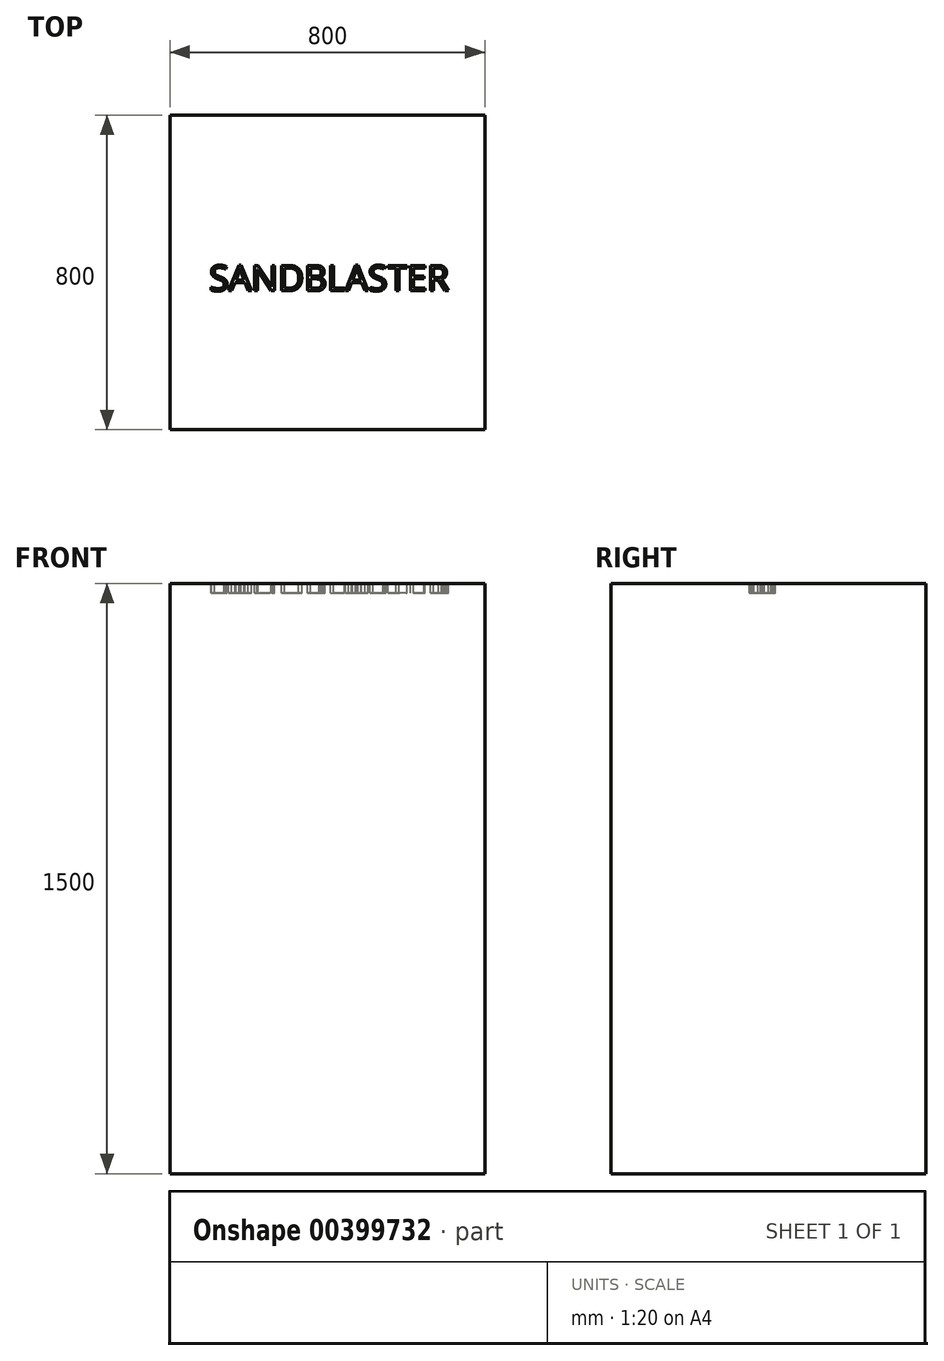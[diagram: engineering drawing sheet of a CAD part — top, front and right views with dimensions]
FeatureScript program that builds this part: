
annotation { "Feature Type Name" : "Feature", "Feature Type Description" : "" }
export const myFeature = defineFeature(function(context is Context, id is Id, definition is map)
    precondition{}
    {
        {
            var Q0;
            Q0=qCreatedBy(makeId("Top.planeOp"),FACE);
            var sketch = newSketch(context, id + "F0", { "sketchPlane" : qUnion([Q0])});
            skLineSegment(sketch, "E0.bottom", {"start": v(400, -400) * mm, "end": v(-400, -400) * mm});
            skLineSegment(sketch, "E0.top", {"start": v(400, 400) * mm, "end": v(-400, 400) * mm});
            skLineSegment(sketch, "E0.left", {"start": v(400, -400) * mm, "end": v(400, 400) * mm});
            skLineSegment(sketch, "E0.right", {"start": v(-400, -400) * mm, "end": v(-400, 400) * mm});
            skPoint(sketch, "E0.middle", {"position": v(0, 0) * mm});
            skSolve(sketch);
        }
        {
            var Q0;
            Q0 = qSketchRegion(id + "F0", true);
            extrude(context, id + "F1", {"entities" : qUnion([Q0]), "depth" : 1500 * mm});
        }
        {
            var Q0;
            Q0=makeQuery(id+"F1.opExtrude","CAP_FACE",FACE,{"disambiguationData":[OSD([sQuery(id+"F0.wireOp",EDGE,"E0.bottom"),sQuery(id+"F0.wireOp",EDGE,"E0.top"),sQuery(id+"F0.wireOp",EDGE,"E0.left"),sQuery(id+"F0.wireOp",EDGE,"E0.right")])],"isStart":false});
            var sketch = newSketch(context, id + "F2", { "sketchPlane" : qUnion([Q0])});
            skText(sketch, "E1", { "text": "SANDBLASTER", "fontName": "OpenSans-Regular.ttf"});
            const initialGuessF2  = {"E1": [-0.3, -0.04692, 1, 0, 0.06502]};
            skSetInitialGuess(sketch, initialGuessF2);
            skSolve(sketch);
        }
        {
            var Q0;
            Q0 = qSketchRegion(id + "F2", true);
            extrude(context, id + "F3", {"entities" : qUnion([Q0]), "operationType" : NewBodyOperationType.REMOVE, "oppositeDirection" : true, "depth" : 25 * mm});
        }
    });
